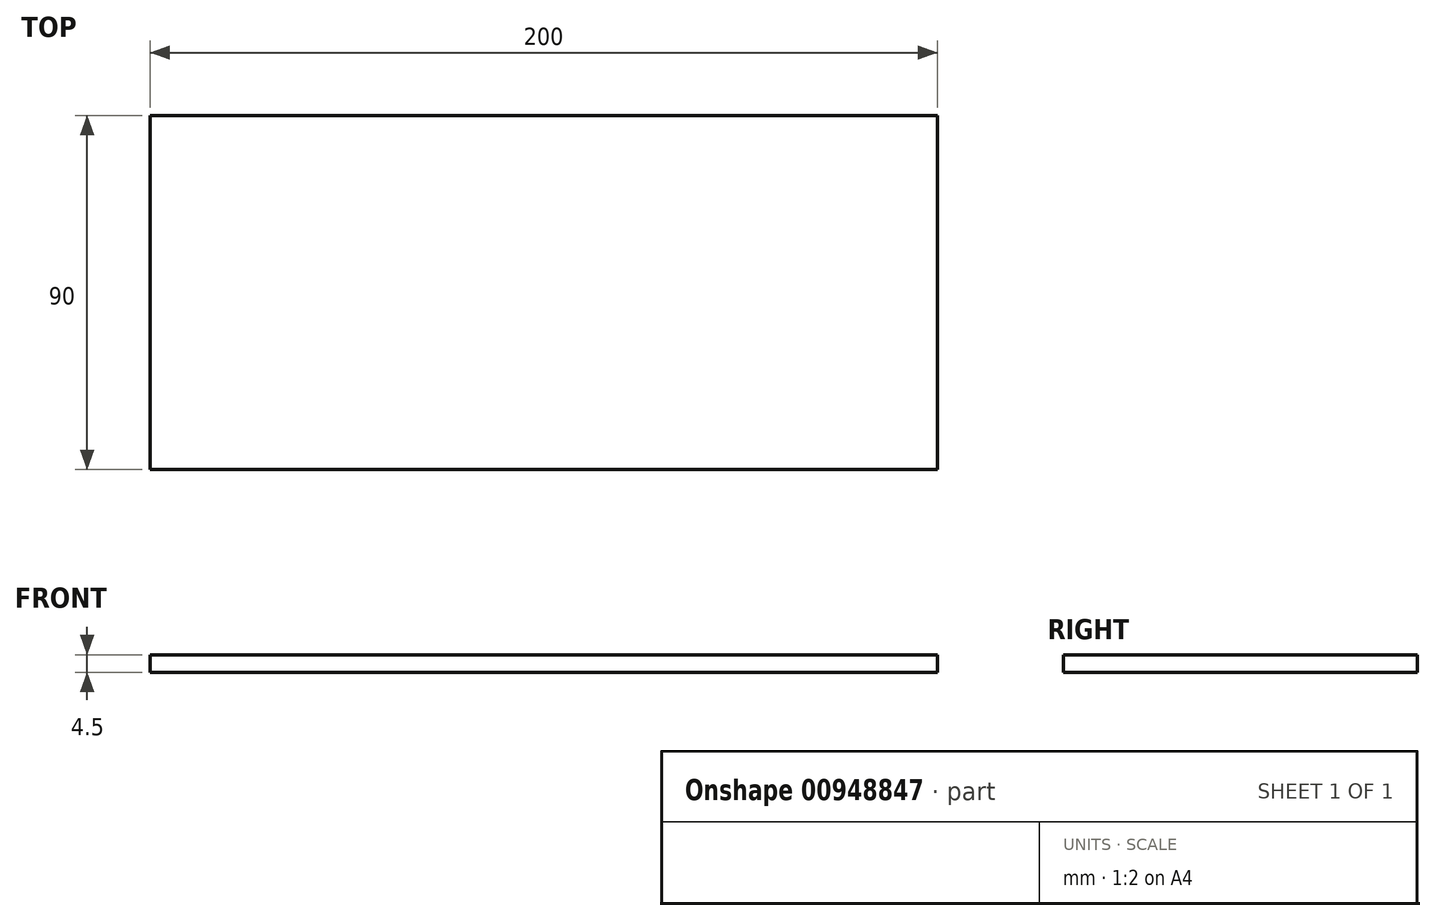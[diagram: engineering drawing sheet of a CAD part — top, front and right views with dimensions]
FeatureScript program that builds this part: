
annotation { "Feature Type Name" : "Feature", "Feature Type Description" : "" }
export const myFeature = defineFeature(function(context is Context, id is Id, definition is map)
    precondition{}
    {
        {
            var Q0;
            Q0=qCreatedBy(makeId("Top.planeOp"),FACE);
            var sketch = newSketch(context, id + "F0", { "sketchPlane" : qUnion([Q0])});
            skLineSegment(sketch, "E0.bottom", {"start": v(100, -45) * mm, "end": v(-100, -45) * mm});
            skLineSegment(sketch, "E0.top", {"start": v(100, 45) * mm, "end": v(-100, 45) * mm});
            skLineSegment(sketch, "E0.left", {"start": v(100, -45) * mm, "end": v(100, 45) * mm});
            skLineSegment(sketch, "E0.right", {"start": v(-100, -45) * mm, "end": v(-100, 45) * mm});
            skPoint(sketch, "E0.middle", {"position": v(0, 0) * mm});
            skSolve(sketch);
        }
        {
            var Q0;
            Q0 = qSketchRegion(id + "F0", true);
            extrude(context, id + "F1", {"entities" : qUnion([Q0]), "depth" : 4.5 * mm, "offsetDistance" : 25 * mm});
        }
    });
